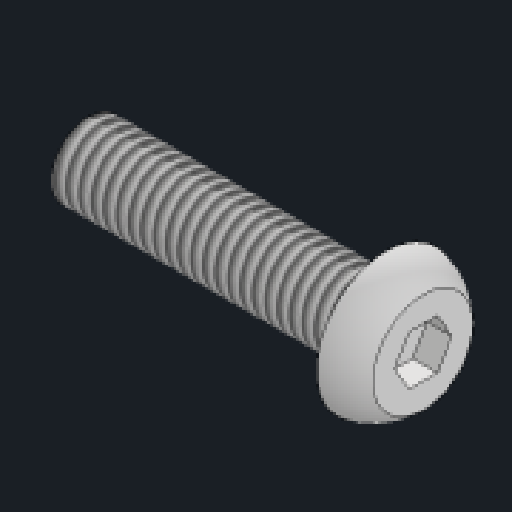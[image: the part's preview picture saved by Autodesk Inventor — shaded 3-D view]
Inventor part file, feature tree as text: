
AUTODESK INVENTOR PART (.ipt)
format: ipt  version: 2023.2 (Build 272271030, 271C)  size: 187,904 bytes
history: native  units: mm
features: sketch x2, revolve x1, thread x1, extrude x1
ambient origin geometry x8: Origin, YZ Plane, XZ Plane, XY Plane, X Axis, Y Axis, Z Axis, Center Point
bodies: Solid1 (feature_tree)
feature tree (5):
  revolve  "Revolution1"  [1 undecoded]
  thread  "Thread1"  [1 undecoded]
  extrude  "Extrusion1"  Depth=0.5mm
  sketch  "Sketch1"  dims[d0=12.0mm d1=1.5mm d2=2.8mm]
  sketch  "Sketch2"  dims[d3=1.5mm d4=0.5mm d5=90.0deg d6=12.0mm d7=0.0mm d8=2.0mm d9=1.0mm d10=0.0mm]
note: 2 required parameter values undecoded (feature->parameter linkage not recoverable at this tier; creation-order binding heuristic only, values carry confidence <= 0.55)